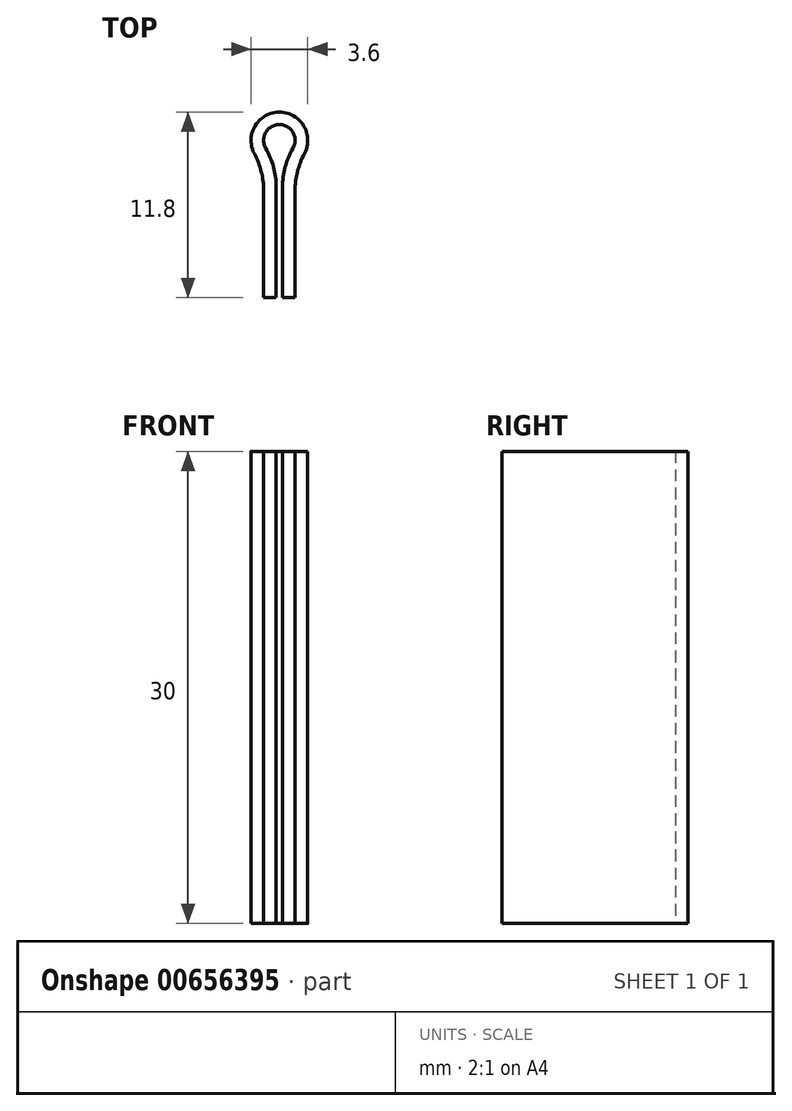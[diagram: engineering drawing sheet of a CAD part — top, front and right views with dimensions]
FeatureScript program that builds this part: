
annotation { "Feature Type Name" : "Feature", "Feature Type Description" : "" }
export const myFeature = defineFeature(function(context is Context, id is Id, definition is map)
    precondition{}
    {
        {
            var Q0;
            Q0=qCreatedBy(makeId("Top.planeOp"),FACE);
            var sketch = newSketch(context, id + "F0", { "sketchPlane" : qUnion([Q0])});
            skLineSegment(sketch, "E0", {"start": v(-0.2, 0) * mm, "end": v(0.2, 0) * mm, "construction": true});
            skLineSegment(sketch, "E1", {"start": v(-0.2, 0) * mm, "end": v(-0.2, 10) * mm});
            skCircle(sketch, "E2", {"center": v(0, 10) * mm, "radius": 1.8 * mm});
            skCircle(sketch, "E3", {"center": v(0, 10) * mm, "radius": 1 * mm});
            skLineSegment(sketch, "E4", {"start": v(0.2, 0) * mm, "end": v(0.2, 10) * mm});
            skLineSegment(sketch, "E5", {"start": v(1, 0) * mm, "end": v(1, 10) * mm});
            skLineSegment(sketch, "E6", {"start": v(-1, 0) * mm, "end": v(-1, 10) * mm});
            skLineSegment(sketch, "E7", {"start": v(-1, 0) * mm, "end": v(-0.2, 0) * mm});
            skLineSegment(sketch, "E8", {"start": v(0.2, 0) * mm, "end": v(1, 0) * mm});
            skSolve(sketch);
        }
        {
            var Q0;
            {var subQ0=sQuery(id+"F0.wireOp",EDGE,"E7");Q0=makeQuery(id+"F0.imprint","IMPRINT",FACE,{"disambiguationData":[TD([[makeQuery(id+"F0.imprint","IMPRINT",EDGE,{"derivedFrom":subQ0}),1.0]])]});}
            var Q1;
            {var subQ0=sQuery(id+"F0.wireOp",EDGE,"E2");var subQ1=sQuery(id+"F0.wireOp",EDGE,"E1");var subQ2=makeQuery(id+"F0.imprint","INTERSECT",VERTEX,{"derivedFrom":[subQ1,subQ0]});Q1=makeQuery(id+"F0.imprint","IMPRINT",FACE,{"disambiguationData":[TD([[makeQuery(id+"F0.imprint","IMPRINT",EDGE,{"disambiguationData":[TD([[subQ2,-1.0]])],"derivedFrom":subQ1}),1.0]])]});}
            var Q2;
            {var subQ0=sQuery(id+"F0.wireOp",EDGE,"E6");var subQ1=sQuery(id+"F0.wireOp",EDGE,"E2");var subQ2=makeQuery(id+"F0.imprint","INTERSECT",VERTEX,{"derivedFrom":[subQ1,subQ0]});Q2=makeQuery(id+"F0.imprint","IMPRINT",FACE,{"disambiguationData":[TD([[makeQuery(id+"F0.imprint","IMPRINT",EDGE,{"disambiguationData":[TD([[subQ2,1.0]])],"derivedFrom":subQ1}),1.0]])]});}
            var Q3;
            {var subQ0=sQuery(id+"F0.wireOp",EDGE,"E4");var subQ1=sQuery(id+"F0.wireOp",EDGE,"E2");var subQ2=makeQuery(id+"F0.imprint","INTERSECT",VERTEX,{"derivedFrom":[subQ1,subQ0]});Q3=makeQuery(id+"F0.imprint","IMPRINT",FACE,{"disambiguationData":[TD([[makeQuery(id+"F0.imprint","IMPRINT",EDGE,{"disambiguationData":[TD([[subQ2,-1.0]])],"derivedFrom":subQ1}),1.0]])]});}
            var Q4;
            {var subQ5=sQuery(id+"F0.wireOp",EDGE,"E8");Q4=makeQuery(id+"F0.imprint","IMPRINT",FACE,{"disambiguationData":[TD([[makeQuery(id+"F0.imprint","IMPRINT",EDGE,{"derivedFrom":subQ5}),1.0]])]});}
            extrude(context, id + "F1", {"entities" : qUnion([Q0, Q1, Q2, Q3, Q4]), "depth" : 30 * mm, "offsetDistance" : 25 * mm});
        }
        {
            var Q0;
            Q0=makeQuery(id+"F1.opExtrude","SWEPT_EDGE",EDGE,{"disambiguationData":[OSD([sQuery(id+"F0.wireOp",EDGE,"E1"),sQuery(id+"F0.wireOp",EDGE,"E3")])]});
            var Q1;
            Q1=makeQuery(id+"F1.opExtrude","SWEPT_EDGE",EDGE,{"disambiguationData":[OSD([sQuery(id+"F0.wireOp",EDGE,"E3"),sQuery(id+"F0.wireOp",EDGE,"E4")])]});
            var Q2;
            Q2=makeQuery(id+"F1.opExtrude","SWEPT_EDGE",EDGE,{"disambiguationData":[OSD([sQuery(id+"F0.wireOp",EDGE,"E2"),sQuery(id+"F0.wireOp",EDGE,"E6")])]});
            var Q3;
            Q3=makeQuery(id+"F1.opExtrude","SWEPT_EDGE",EDGE,{"disambiguationData":[OSD([sQuery(id+"F0.wireOp",EDGE,"E2"),sQuery(id+"F0.wireOp",EDGE,"E5")])]});
            fillet(context, id + "F2", {"entities" : qUnion([Q0, Q1, Q2, Q3]), "radius" : 5 * mm, "tangentPropagation" : true, "allowEdgeOverflow" : false});
        }
    });
